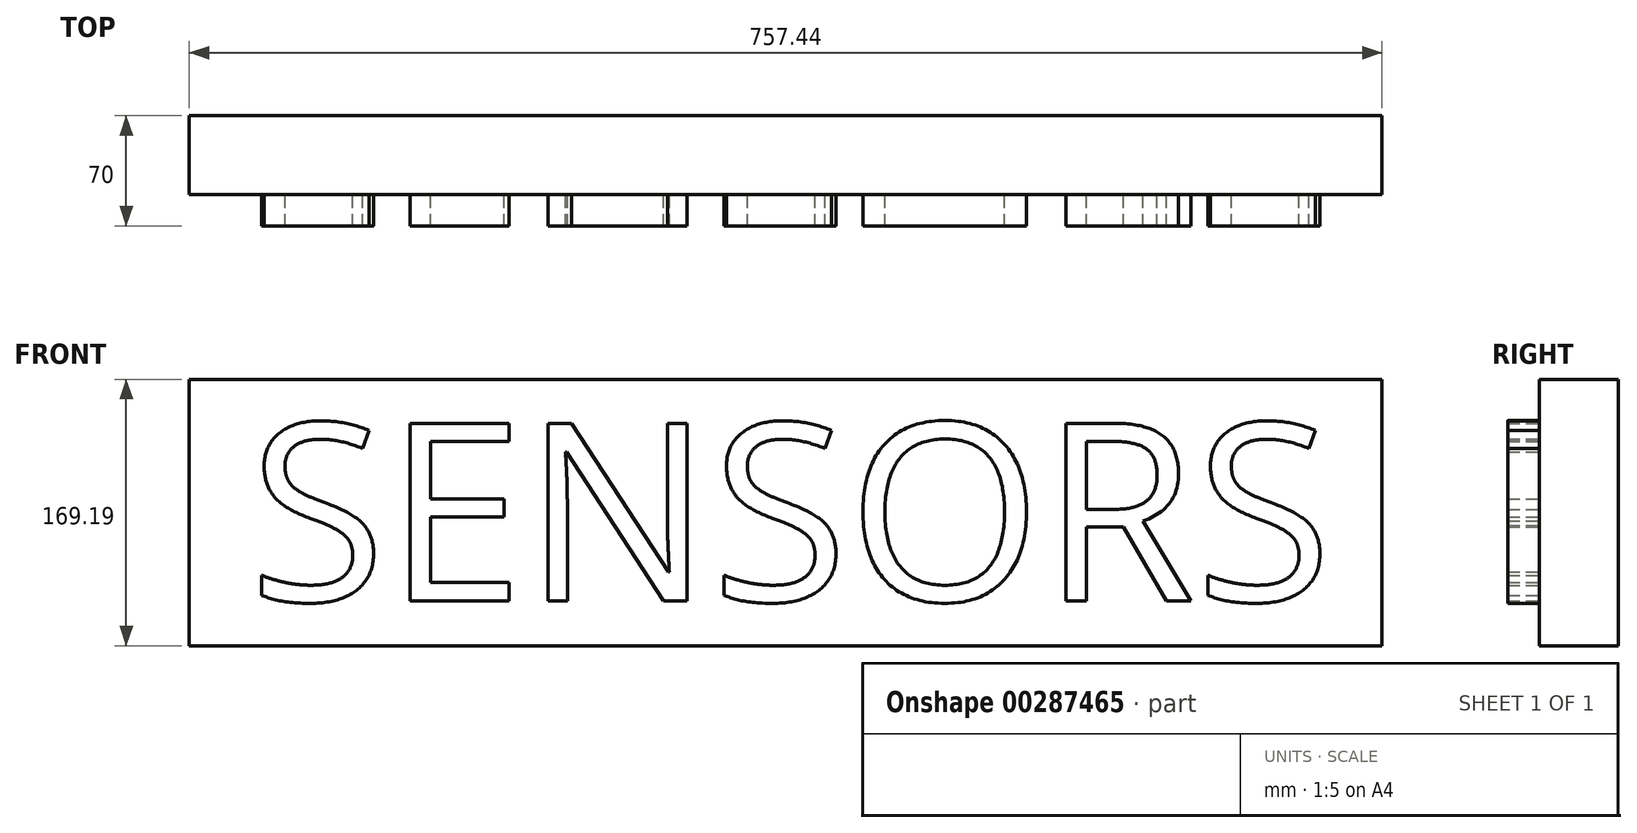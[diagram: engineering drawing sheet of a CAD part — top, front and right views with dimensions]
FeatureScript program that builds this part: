
annotation { "Feature Type Name" : "Feature", "Feature Type Description" : "" }
export const myFeature = defineFeature(function(context is Context, id is Id, definition is map)
    precondition{}
    {
        {
            var Q0;
            Q0=qCreatedBy(makeId("Front.planeOp"),FACE);
            var sketch = newSketch(context, id + "F0", { "sketchPlane" : qUnion([Q0])});
            skLineSegment(sketch, "E0.bottom", {"start": v(0, 0) * mm, "end": v(757.44, 0) * mm});
            skLineSegment(sketch, "E0.top", {"start": v(0, 169.2) * mm, "end": v(757.44, 169.2) * mm});
            skLineSegment(sketch, "E0.left", {"start": v(0, 0) * mm, "end": v(0, 169.2) * mm});
            skLineSegment(sketch, "E0.right", {"start": v(757.44, 0) * mm, "end": v(757.44, 169.2) * mm});
            skSolve(sketch);
        }
        {
            var Q0;
            Q0=qSketchRegion(id+"F0",true);
            extrude(context, id + "F1", {"entities" : qUnion([Q0]), "depth" : 50 * mm});
        }
        {
            var Q0;
            Q0=qCreatedBy(makeId("Front.planeOp"),FACE);
            var sketch = newSketch(context, id + "F2", { "sketchPlane" : qUnion([Q0])});
            skText(sketch, "E1", { "text": "SENSORS", "fontName": "OpenSans-Regular.ttf"});
            const initialGuessF2  = {"E1": [0.03787, 0.02852, 1, 0, 0.11374]};
            skSetInitialGuess(sketch, initialGuessF2);
            skSolve(sketch);
        }
        {
            var Q0;
            Q0=qSketchRegion(id+"F2",true);
            extrude(context, id + "F3", {"entities" : qUnion([Q0]), "operationType" : NewBodyOperationType.ADD, "depth" : 70 * mm});
        }
    });
